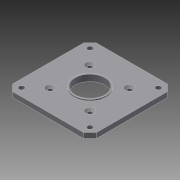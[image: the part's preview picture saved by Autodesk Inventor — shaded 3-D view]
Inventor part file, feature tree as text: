
AUTODESK INVENTOR PART (.ipt)
format: ipt  version: 2021.3 (Build 253353000, 353)  size: 156,160 bytes
history: native  units: mm
features: other x6, reference x5, sketch x4, extrude x2, hole x2
ambient origin geometry x8: Origin, YZ Plane, XZ Plane, XY Plane, X Axis, Y Axis, Z Axis, Center Point
bodies: Body1 (feature_tree)
feature tree (19):
  other  "Твердое тело1"
  other  "РабПлоскость1"
  extrude  "Выдавливание1"  Depth=65.0mm
  hole  "Отверстие1"  [1 undecoded]
  hole  "Отверстие2"  [1 undecoded]
  extrude  "Выдавливание2"  Depth=5.0mm
  sketch  "Эскиз1"
  reference  "Ссылка1"
  reference  "Ссылка2"
  reference  "Ссылка3"
  reference  "Ссылка4"
  reference  "Ссылка5"
  sketch  "Эскиз2"
  sketch  "Эскиз3"
  sketch  "Эскиз4"
  parser-record x1  (decoder bookkeeping rows leaked as tree rows — omitted from the tree; the rows remain in map.json)
  other  "Nema17.iam"
  other  "Pumpshare:1"
  other  "Top:1"
note: 2 required parameter values undecoded (feature->parameter linkage not recoverable at this tier; creation-order binding heuristic only, values carry confidence <= 0.55)
note: 1 file-system path scrubbed to <path> (originals preserved in map.json)
